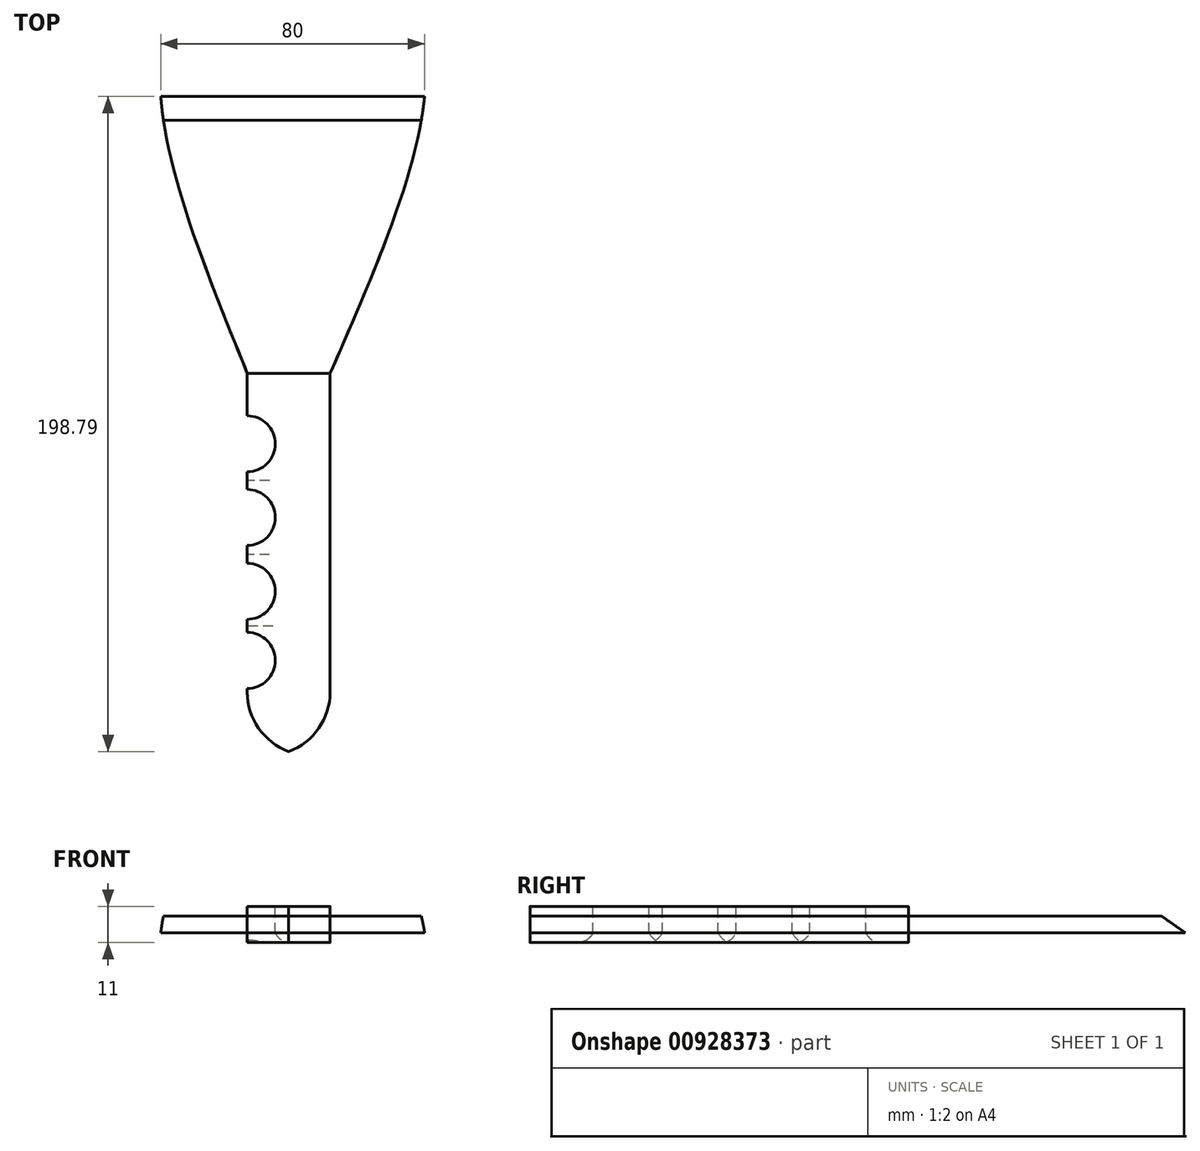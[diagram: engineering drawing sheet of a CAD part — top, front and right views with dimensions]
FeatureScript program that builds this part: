
annotation { "Feature Type Name" : "Feature", "Feature Type Description" : "" }
export const myFeature = defineFeature(function(context is Context, id is Id, definition is map)
    precondition{}
    {
        {
            var Q0;
            Q0=qCreatedBy(makeId("Top.planeOp"),FACE);
            var sketch = newSketch(context, id + "F0", { "sketchPlane" : qUnion([Q0])});
            skLineSegment(sketch, "E0.bottom", {"start": v(-41.5, 154.32) * mm, "end": v(38.5, 154.32) * mm});
            skLineSegment(sketch, "E0.top", {"start": v(-41.5, -45.68) * mm, "end": v(38.5, -45.68) * mm});
            skLineSegment(sketch, "E0.left", {"start": v(-41.5, 154.32) * mm, "end": v(-41.5, -45.68) * mm});
            skLineSegment(sketch, "E0.right", {"start": v(38.5, 154.32) * mm, "end": v(38.5, -45.68) * mm});
            skLineSegment(sketch, "E1", {"start": v(-15.28, 154.32) * mm, "end": v(-15.28, -45.68) * mm});
            skLineSegment(sketch, "E2", {"start": v(9.87, 154.32) * mm, "end": v(9.87, -45.68) * mm});
            skLineSegment(sketch, "E3", {"start": v(-41.5, 70.36) * mm, "end": v(38.5, 70.36) * mm});
            skFitSpline(sketch, "E4", {"points": [v(-15.28, 70.36) * mm, v(-41.5, 154.32) * mm, v(-34.52, 196.12) * mm], "startDerivative": vector(-62.55, 154.1) * mm, "endDerivative": vector(29.63, 93.77) * mm});
            skFitSpline(sketch, "E5", {"points": [v(9.87, 70.36) * mm, v(38.5, 154.32) * mm, v(32.43, 196.86) * mm], "startDerivative": vector(67.24, 153.82) * mm, "endDerivative": vector(-27.8, 95.7) * mm});
            skSolve(sketch);
        }
        {
            var Q0;
            {var subQ1=sQuery(id+"F0.wireOp",EDGE,"E0.bottom");var subQ3=sQuery(id+"F0.wireOp",EDGE,"E1");var subQ4=makeQuery(id+"F0.imprint","INTERSECT",VERTEX,{"derivedFrom":[subQ1,subQ3]});Q0=makeQuery(id+"F0.imprint","IMPRINT",FACE,{"disambiguationData":[TD([[makeQuery(id+"F0.imprint","IMPRINT",EDGE,{"disambiguationData":[TD([[subQ4,1.0]])],"derivedFrom":subQ1}),-1.0]])]});}
            var Q1;
            {var subQ0=sQuery(id+"F0.wireOp",EDGE,"E1");var subQ1=sQuery(id+"F0.wireOp",EDGE,"E0.bottom");var subQ2=makeQuery(id+"F0.imprint","INTERSECT",VERTEX,{"derivedFrom":[subQ1,subQ0]});Q1=makeQuery(id+"F0.imprint","IMPRINT",FACE,{"disambiguationData":[TD([[makeQuery(id+"F0.imprint","IMPRINT",EDGE,{"disambiguationData":[TD([[subQ2,-1.0]])],"derivedFrom":subQ1}),-1.0]])]});}
            var Q2;
            {var subQ1=sQuery(id+"F0.wireOp",EDGE,"E0.bottom");var subQ3=sQuery(id+"F0.wireOp",EDGE,"E2");var subQ4=makeQuery(id+"F0.imprint","INTERSECT",VERTEX,{"derivedFrom":[subQ1,subQ3]});Q2=makeQuery(id+"F0.imprint","IMPRINT",FACE,{"disambiguationData":[TD([[makeQuery(id+"F0.imprint","IMPRINT",EDGE,{"disambiguationData":[TD([[subQ4,-1.0]])],"derivedFrom":subQ1}),-1.0]])]});}
            var Q3;
            {var subQ0=sQuery(id+"F0.wireOp",EDGE,"E1");var subQ1=sQuery(id+"F0.wireOp",EDGE,"E0.top");var subQ2=makeQuery(id+"F0.imprint","INTERSECT",VERTEX,{"derivedFrom":[subQ1,subQ0]});Q3=makeQuery(id+"F0.imprint","IMPRINT",FACE,{"disambiguationData":[TD([[makeQuery(id+"F0.imprint","IMPRINT",EDGE,{"disambiguationData":[TD([[subQ2,-1.0]])],"derivedFrom":subQ1}),1.0]])]});}
            extrude(context, id + "F1", {"entities" : qUnion([Q0, Q1, Q2, Q3]), "depth" : 5 * mm, "offsetDistance" : 25 * mm});
        }
        {
            var Q0;
            Q0=makeQuery(id+"F1.opExtrude","CAP_FACE",FACE,{"disambiguationData":[OSD([sQuery(id+"F0.wireOp",EDGE,"E0.bottom"),sQuery(id+"F0.wireOp",EDGE,"E0.top"),sQuery(id+"F0.wireOp",EDGE,"E1"),sQuery(id+"F0.wireOp",EDGE,"E2"),sQuery(id+"F0.wireOp",EDGE,"E4"),sQuery(id+"F0.wireOp",EDGE,"E5")])],"isStart":false});
            var sketch = newSketch(context, id + "F2", { "sketchPlane" : qUnion([Q0])});
            skLineSegment(sketch, "E6", {"start": v(-15.28, 70.36) * mm, "end": v(9.87, 70.36) * mm});
            skSolve(sketch);
        }
        {
            var Q0;
            Q0 = qSketchRegion(id + "F2", true);
            var Q1;
            Q1=makeQuery(id+"F2.imprint","IMPRINT",FACE,{"disambiguationData":[TD([[makeQuery(id+"F2.imprint","IMPRINT",EDGE,{"derivedFrom":sQuery(id+"F2.wireOp",EDGE,"E6")}),-1.0]])]});
            extrude(context, id + "F3", {"entities" : qUnion([Q0, Q1]), "depth" : 3 * mm, "offsetDistance" : 25 * mm});
        }
        {
            var Q0;
            Q0=makeQuery(id+"F1.opExtrude","CAP_FACE",FACE,{"disambiguationData":[OSD([sQuery(id+"F0.wireOp",EDGE,"E0.bottom"),sQuery(id+"F0.wireOp",EDGE,"E0.top"),sQuery(id+"F0.wireOp",EDGE,"E1"),sQuery(id+"F0.wireOp",EDGE,"E2"),sQuery(id+"F0.wireOp",EDGE,"E4"),sQuery(id+"F0.wireOp",EDGE,"E5")])],"isStart":true});
            var sketch = newSketch(context, id + "F4", { "sketchPlane" : qUnion([Q0])});
            skLineSegment(sketch, "E7", {"start": v(9.87, -70.36) * mm, "end": v(-15.28, -70.36) * mm});
            skSolve(sketch);
        }
        {
            var Q0;
            Q0 = qSketchRegion(id + "F4", true);
            var Q1;
            Q1=makeQuery(id+"F4.imprint","IMPRINT",FACE,{"disambiguationData":[TD([[makeQuery(id+"F4.imprint","IMPRINT",EDGE,{"derivedFrom":sQuery(id+"F4.wireOp",EDGE,"E7")}),-1.0]])]});
            extrude(context, id + "F5", {"entities" : qUnion([Q0, Q1]), "depth" : 3 * mm, "offsetDistance" : 25 * mm});
        }
        {
            var Q0;
            Q0=makeQuery(id+"F1.opExtrude","SWEPT_EDGE",EDGE,{"disambiguationData":[OSD([sQuery(id+"F0.wireOp",EDGE,"E0.top"),sQuery(id+"F0.wireOp",EDGE,"E1")])]});
            var Q1;
            Q1=makeQuery(id+"F5.opExtrude","SWEPT_EDGE",EDGE,{"disambiguationData":[OSD([sQuery(id+"F0.wireOp",EDGE,"E0.top"),sQuery(id+"F0.wireOp",EDGE,"E1")])]});
            var Q2;
            Q2=makeQuery(id+"F3.opExtrude","SWEPT_EDGE",EDGE,{"disambiguationData":[OSD([sQuery(id+"F0.wireOp",EDGE,"E0.top"),sQuery(id+"F0.wireOp",EDGE,"E1")])]});
            var Q3;
            Q3=makeQuery(id+"F3.opExtrude","SWEPT_EDGE",EDGE,{"disambiguationData":[OSD([sQuery(id+"F0.wireOp",EDGE,"E0.top"),sQuery(id+"F0.wireOp",EDGE,"E2")])]});
            var Q4;
            Q4=makeQuery(id+"F1.opExtrude","SWEPT_EDGE",EDGE,{"disambiguationData":[OSD([sQuery(id+"F0.wireOp",EDGE,"E0.top"),sQuery(id+"F0.wireOp",EDGE,"E2")])]});
            var Q5;
            Q5=makeQuery(id+"F5.opExtrude","SWEPT_EDGE",EDGE,{"disambiguationData":[OSD([sQuery(id+"F0.wireOp",EDGE,"E0.top"),sQuery(id+"F0.wireOp",EDGE,"E2")])]});
            fillet(context, id + "F6", {"entities" : qUnion([Q0, Q1, Q2, Q3, Q4, Q5]), "radius" : 19.3 * mm, "tangentPropagation" : true, "allowEdgeOverflow" : false});
        }
        {
            var Q0;
            Q0=makeQuery(id+"F3.opExtrude","CAP_FACE",FACE,{"disambiguationData":[OSD([sQuery(id+"F0.wireOp",EDGE,"E0.top"),sQuery(id+"F0.wireOp",EDGE,"E1"),sQuery(id+"F0.wireOp",EDGE,"E2"),sQuery(id+"F2.wireOp",EDGE,"E6")])],"isStart":false});
            var sketch = newSketch(context, id + "F7", { "sketchPlane" : qUnion([Q0])});
            skCircle(sketch, "E8", {"center": v(-15.28, 48.94) * mm, "radius": 8.5 * mm});
            skCircle(sketch, "E9", {"center": v(-15.28, 26.57) * mm, "radius": 8.5 * mm});
            skCircle(sketch, "E10", {"center": v(-15.28, 4.14) * mm, "radius": 8.5 * mm});
            skCircle(sketch, "E11", {"center": v(-15.28, -16.83) * mm, "radius": 8.5 * mm});
            skSolve(sketch);
        }
        {
            var Q0;
            {var subQ0=sQuery(id+"F7.wireOp",EDGE,"E11");var subQ1=makeQuery(id+"F3.opExtrude","CAP_EDGE",EDGE,{"disambiguationData":[OSD([sQuery(id+"F0.wireOp",EDGE,"E1")])],"isStart":false});var subQ2=makeQuery(id+"F7.imprint","INTERSECT",VERTEX,{"disambiguationData":[OD(0.0)],"derivedFrom":[subQ1,subQ0]});Q0=makeQuery(id+"F7.imprint","IMPRINT",FACE,{"disambiguationData":[TD([[makeQuery(id+"F7.imprint","IMPRINT",EDGE,{"disambiguationData":[TD([[subQ2,-1.0]])],"derivedFrom":subQ0}),1.0]])]});}
            var Q1;
            {var subQ0=sQuery(id+"F7.wireOp",EDGE,"E10");var subQ1=makeQuery(id+"F3.opExtrude","CAP_EDGE",EDGE,{"disambiguationData":[OSD([sQuery(id+"F0.wireOp",EDGE,"E1")])],"isStart":false});var subQ2=makeQuery(id+"F7.imprint","INTERSECT",VERTEX,{"disambiguationData":[OD(0.0)],"derivedFrom":[subQ1,subQ0]});Q1=makeQuery(id+"F7.imprint","IMPRINT",FACE,{"disambiguationData":[TD([[makeQuery(id+"F7.imprint","IMPRINT",EDGE,{"disambiguationData":[TD([[subQ2,-1.0]])],"derivedFrom":subQ0}),1.0]])]});}
            var Q2;
            {var subQ0=sQuery(id+"F7.wireOp",EDGE,"E9");var subQ1=makeQuery(id+"F3.opExtrude","CAP_EDGE",EDGE,{"disambiguationData":[OSD([sQuery(id+"F0.wireOp",EDGE,"E1")])],"isStart":false});var subQ2=makeQuery(id+"F7.imprint","INTERSECT",VERTEX,{"disambiguationData":[OD(0.0)],"derivedFrom":[subQ1,subQ0]});Q2=makeQuery(id+"F7.imprint","IMPRINT",FACE,{"disambiguationData":[TD([[makeQuery(id+"F7.imprint","IMPRINT",EDGE,{"disambiguationData":[TD([[subQ2,1.0]])],"derivedFrom":subQ0}),1.0]])]});}
            var Q3;
            {var subQ0=sQuery(id+"F7.wireOp",EDGE,"E8");var subQ1=makeQuery(id+"F3.opExtrude","CAP_EDGE",EDGE,{"disambiguationData":[OSD([sQuery(id+"F0.wireOp",EDGE,"E1")])],"isStart":false});var subQ2=makeQuery(id+"F7.imprint","INTERSECT",VERTEX,{"disambiguationData":[OD(0.0)],"derivedFrom":[subQ1,subQ0]});Q3=makeQuery(id+"F7.imprint","IMPRINT",FACE,{"disambiguationData":[TD([[makeQuery(id+"F7.imprint","IMPRINT",EDGE,{"disambiguationData":[TD([[subQ2,1.0]])],"derivedFrom":subQ0}),1.0]])]});}
            extrude(context, id + "F8", {"entities" : qUnion([Q0, Q1, Q2, Q3]), "operationType" : NewBodyOperationType.ADD, "depth" : 25 * mm, "offsetDistance" : 25 * mm});
        }
        {
            var Q0;
            Q0=makeQuery(id+"F8.opExtrude","CAP_FACE",FACE,{"disambiguationData":[OSD([sQuery(id+"F0.wireOp",EDGE,"E1"),sQuery(id+"F7.wireOp",EDGE,"E11")])],"isStart":false});
            var Q1;
            Q1=makeQuery(id+"F8.opExtrude","CAP_FACE",FACE,{"disambiguationData":[OSD([sQuery(id+"F0.wireOp",EDGE,"E1"),sQuery(id+"F7.wireOp",EDGE,"E10")])],"isStart":false});
            var Q2;
            Q2=makeQuery(id+"F8.opExtrude","CAP_FACE",FACE,{"disambiguationData":[OSD([sQuery(id+"F0.wireOp",EDGE,"E1"),sQuery(id+"F7.wireOp",EDGE,"E9")])],"isStart":false});
            var Q3;
            Q3=makeQuery(id+"F8.opExtrude","CAP_FACE",FACE,{"disambiguationData":[OSD([sQuery(id+"F0.wireOp",EDGE,"E1"),sQuery(id+"F7.wireOp",EDGE,"E8")])],"isStart":false});
            extrude(context, id + "F9", {"entities" : qUnion([Q0, Q1, Q2, Q3]), "operationType" : NewBodyOperationType.REMOVE, "oppositeDirection" : true, "depth" : 70 * mm, "offsetDistance" : 25 * mm});
        }
        {
            var Q0;
            Q0=makeQuery(id+"F8.opExtrude","CAP_EDGE",EDGE,{"disambiguationData":[OSD([sQuery(id+"F7.wireOp",EDGE,"E8")])],"isStart":true});
            var Q1;
            Q1=makeQuery(id+"F8.opExtrude","CAP_EDGE",EDGE,{"disambiguationData":[OSD([sQuery(id+"F7.wireOp",EDGE,"E9")])],"isStart":true});
            var Q2;
            Q2=makeQuery(id+"F8.opExtrude","CAP_EDGE",EDGE,{"disambiguationData":[OSD([sQuery(id+"F7.wireOp",EDGE,"E10")])],"isStart":true});
            var Q3;
            Q3=makeQuery(id+"F8.opExtrude","CAP_EDGE",EDGE,{"disambiguationData":[OSD([sQuery(id+"F7.wireOp",EDGE,"E11")])],"isStart":true});
            var Q4;
            Q4=makeQuery(id+"F9.boolean.opBoolean","INTERSECT",EDGE,{"derivedFrom":[makeQuery(id+"F5.opExtrude","CAP_FACE",FACE,{"disambiguationData":[OSD([sQuery(id+"F0.wireOp",EDGE,"E0.top"),sQuery(id+"F0.wireOp",EDGE,"E1"),sQuery(id+"F0.wireOp",EDGE,"E2"),sQuery(id+"F4.wireOp",EDGE,"E7")])],"isStart":false}),makeQuery(id+"F9.opExtrude","SWEPT_FACE",FACE,{"disambiguationData":[OSD([sQuery(id+"F7.wireOp",EDGE,"E11")])]})]});
            var Q5;
            Q5=makeQuery(id+"F9.boolean.opBoolean","INTERSECT",EDGE,{"derivedFrom":[makeQuery(id+"F5.opExtrude","CAP_FACE",FACE,{"disambiguationData":[OSD([sQuery(id+"F0.wireOp",EDGE,"E0.top"),sQuery(id+"F0.wireOp",EDGE,"E1"),sQuery(id+"F0.wireOp",EDGE,"E2"),sQuery(id+"F4.wireOp",EDGE,"E7")])],"isStart":false}),makeQuery(id+"F9.opExtrude","SWEPT_FACE",FACE,{"disambiguationData":[OSD([sQuery(id+"F7.wireOp",EDGE,"E10")])]})]});
            var Q6;
            Q6=makeQuery(id+"F9.boolean.opBoolean","INTERSECT",EDGE,{"derivedFrom":[makeQuery(id+"F5.opExtrude","CAP_FACE",FACE,{"disambiguationData":[OSD([sQuery(id+"F0.wireOp",EDGE,"E0.top"),sQuery(id+"F0.wireOp",EDGE,"E1"),sQuery(id+"F0.wireOp",EDGE,"E2"),sQuery(id+"F4.wireOp",EDGE,"E7")])],"isStart":false}),makeQuery(id+"F9.opExtrude","SWEPT_FACE",FACE,{"disambiguationData":[OSD([sQuery(id+"F7.wireOp",EDGE,"E9")])]})]});
            var Q7;
            Q7=makeQuery(id+"F9.boolean.opBoolean","INTERSECT",EDGE,{"derivedFrom":[makeQuery(id+"F5.opExtrude","CAP_FACE",FACE,{"disambiguationData":[OSD([sQuery(id+"F0.wireOp",EDGE,"E0.top"),sQuery(id+"F0.wireOp",EDGE,"E1"),sQuery(id+"F0.wireOp",EDGE,"E2"),sQuery(id+"F4.wireOp",EDGE,"E7")])],"isStart":false}),makeQuery(id+"F9.opExtrude","SWEPT_FACE",FACE,{"disambiguationData":[OSD([sQuery(id+"F7.wireOp",EDGE,"E8")])]})]});
            fillet(context, id + "F10", {"entities" : qUnion([Q0, Q1, Q2, Q3, Q4, Q5, Q6, Q7]), "radius" : 5 * mm, "tangentPropagation" : true, "allowEdgeOverflow" : false});
        }
        {
            var Q0;
            Q0=makeQuery(id+"F3.opExtrude","CAP_EDGE",EDGE,{"disambiguationData":[OSD([sQuery(id+"F0.wireOp",EDGE,"E2")])],"isStart":false});
            var Q1;
            Q1=makeQuery(id+"F5.opExtrude","CAP_EDGE",EDGE,{"disambiguationData":[OSD([sQuery(id+"F0.wireOp",EDGE,"E2")])],"isStart":false});
            var Q2;
            {var subQ0=sQuery(id+"F0.wireOp",EDGE,"E1");var subQ1=sQuery(id+"F0.wireOp",EDGE,"E0.top");Q2=makeQuery(id+"F6.opFillet","BLEND_EDGE",EDGE,{"blendedFrom":[makeQuery(id+"F5.opExtrude","SWEPT_EDGE",EDGE,{"disambiguationData":[OSD([subQ1,subQ0])]}),makeQuery(id+"F5.opExtrude","CAP_FACE",FACE,{"disambiguationData":[OSD([subQ1,subQ0,sQuery(id+"F0.wireOp",EDGE,"E2"),sQuery(id+"F4.wireOp",EDGE,"E7")])],"isStart":false})],"blendedInto":[makeQuery(id+"F5.opExtrude","CAP_FACE",FACE,{"disambiguationData":[OSD([subQ1,subQ0,sQuery(id+"F0.wireOp",EDGE,"E2"),sQuery(id+"F4.wireOp",EDGE,"E7")])],"isStart":false})]});}
            fillet(context, id + "F11", {"entities" : qUnion([Q0, Q1, Q2]), "radius" : 0.02 * mm, "tangentPropagation" : true, "allowEdgeOverflow" : false});
        }
        {
            var Q0;
            Q0=makeQuery(id+"F1.opExtrude","CAP_EDGE",EDGE,{"disambiguationData":[OSD([sQuery(id+"F0.wireOp",EDGE,"E0.bottom")])],"isStart":false});
            chamfer(context, id + "F12", {"entities" : qUnion([Q0]), "chamferType" : ChamferType.OFFSET_ANGLE, "width" : 5 * mm, "oppositeDirection" : false, "angle" : 55 * degree, "tangentPropagation" : true});
        }
    });
